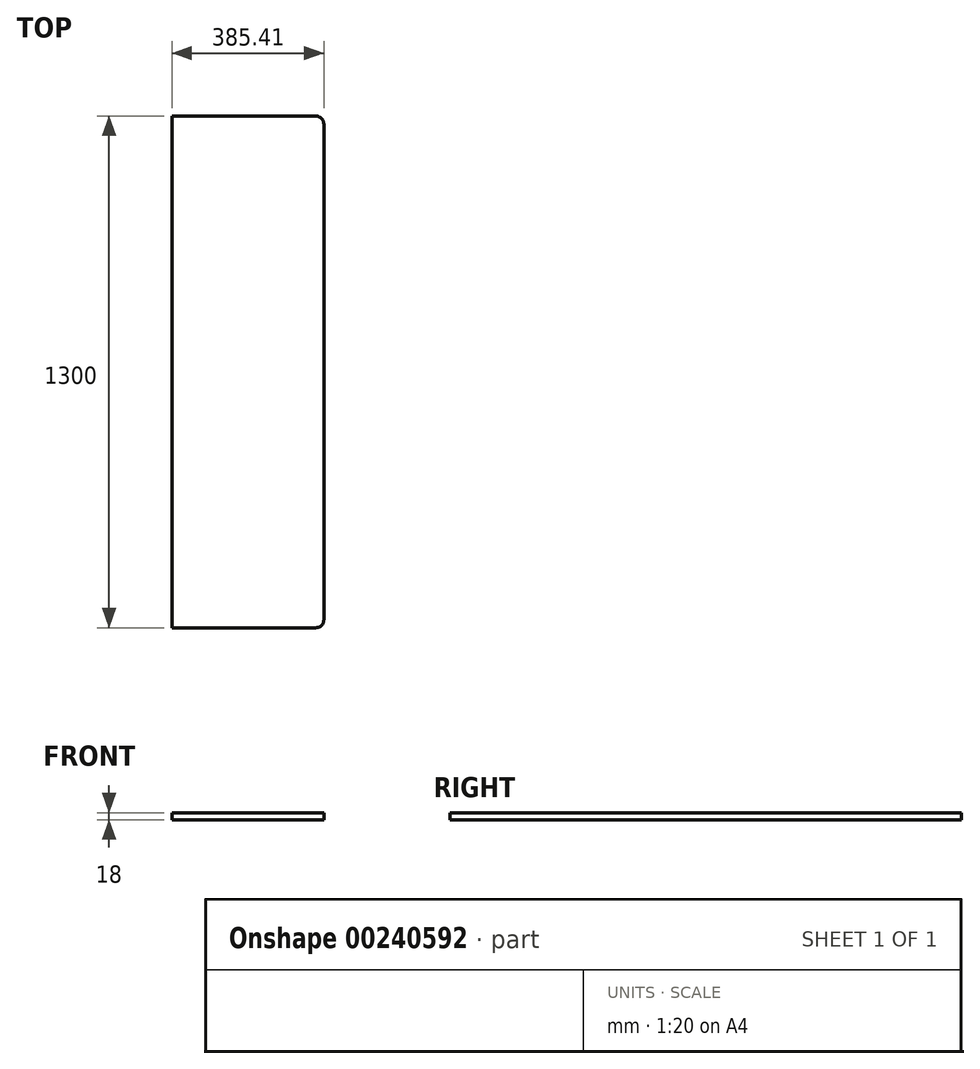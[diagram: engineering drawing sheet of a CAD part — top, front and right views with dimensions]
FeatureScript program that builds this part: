
annotation { "Feature Type Name" : "Feature", "Feature Type Description" : "" }
export const myFeature = defineFeature(function(context is Context, id is Id, definition is map)
    precondition{}
    {
        {
            var Q0;
            Q0=qCreatedBy(makeId("Top.planeOp"),FACE);
            var sketch = newSketch(context, id + "F0", { "sketchPlane" : qUnion([Q0])});
            skLineSegment(sketch, "E0.bottom", {"start": v(0, 0) * mm, "end": v(385.41, 0) * mm});
            skLineSegment(sketch, "E0.top", {"start": v(0, 1300) * mm, "end": v(385.41, 1300) * mm});
            skLineSegment(sketch, "E0.left", {"start": v(0, 0) * mm, "end": v(0, 1300) * mm});
            skLineSegment(sketch, "E0.right", {"start": v(385.41, 0) * mm, "end": v(385.41, 1300) * mm});
            skSolve(sketch);
        }
        {
            var Q0;
            Q0 = qSketchRegion(id + "F0", true);
            extrude(context, id + "F1", {"entities" : qUnion([Q0]), "depth" : 18 * mm});
        }
        {
            var Q0;
            Q0=makeQuery(id+"F1.opExtrude","SWEPT_EDGE",EDGE,{"disambiguationData":[OSD([sQuery(id+"F0.wireOp",EDGE,"E0.bottom"),sQuery(id+"F0.wireOp",EDGE,"E0.right")])]});
            var Q1;
            Q1=makeQuery(id+"F1.opExtrude","SWEPT_EDGE",EDGE,{"disambiguationData":[OSD([sQuery(id+"F0.wireOp",EDGE,"E0.top"),sQuery(id+"F0.wireOp",EDGE,"E0.right")])]});
            fillet(context, id + "F2", {"entities" : qUnion([Q0, Q1]), "radius" : 20 * mm, "tangentPropagation" : true, "allowEdgeOverflow" : false});
        }
    });
